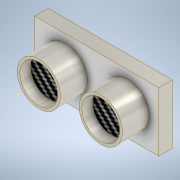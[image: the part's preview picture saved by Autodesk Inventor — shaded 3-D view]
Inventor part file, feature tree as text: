
AUTODESK INVENTOR PART (.ipt)
format: ipt  version: 2021 (Build 250183000, 183)  size: 144,896 bytes
history: native  units: mm
features: sketch x6, extrude x4
ambient origin geometry x8: Origin, YZ Plane, XZ Plane, XY Plane, X Axis, Y Axis, Z Axis, Center Point
bodies: Solid1 (feature_tree)
feature tree (10):
  extrude  "Extrusion1"  Depth=22.0mm
  extrude  "Extrusion2"  Depth=5.0mm
  sketch  "Sketch3"  dims[d5=16.0mm d6=10.0mm d7=0.0mm]
  sketch  "Sketch4"  dims[d8=14.0mm d9=14.0mm]
  extrude  "Extrusion3"  Depth=10.0mm TaperAngle=0.0deg
  extrude  "Extrusion4"  Depth=14.0mm
  sketch  "Sketch5"  dims[d10=4.0mm d11=0.0mm]
  sketch  "Sketch6"  dims[d12=4.0mm d13=0.0mm]
  sketch  "Sketch1"  dims[d0=46.0mm d1=22.0mm]
  sketch  "Sketch2"  dims[d2=5.0mm d3=0.0mm d4=16.0mm]
